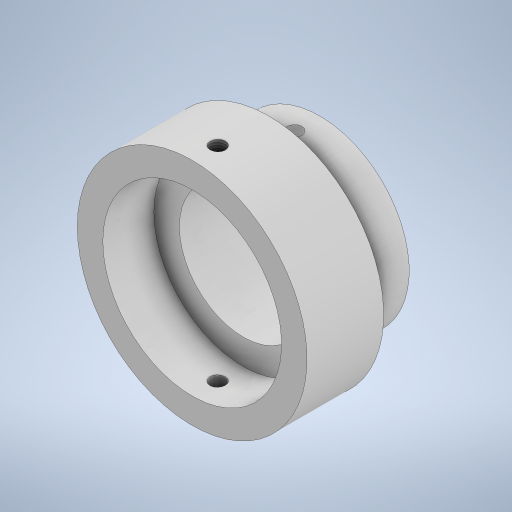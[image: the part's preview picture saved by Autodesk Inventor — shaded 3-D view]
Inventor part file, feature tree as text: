
AUTODESK INVENTOR PART (.ipt)
format: ipt  version: 2023 (Build 270158000, 158)  size: 293,888 bytes
history: native  units: mm
features: thread x2, sketch x2, revolve x1, extrude x1
ambient origin geometry x8: Origin, YZ Plane, XZ Plane, XY Plane, X Axis, Y Axis, Z Axis, Center Point
bodies: Body1 (feature_tree)
feature tree (6):
  revolve  "Вращение1"
  extrude  "Выдавливание3"  Depth=10.0mm
  thread  "Резьба1"
  thread  "Резьба2"
  sketch  "Эскиз1"
  sketch  "Эскиз4"
